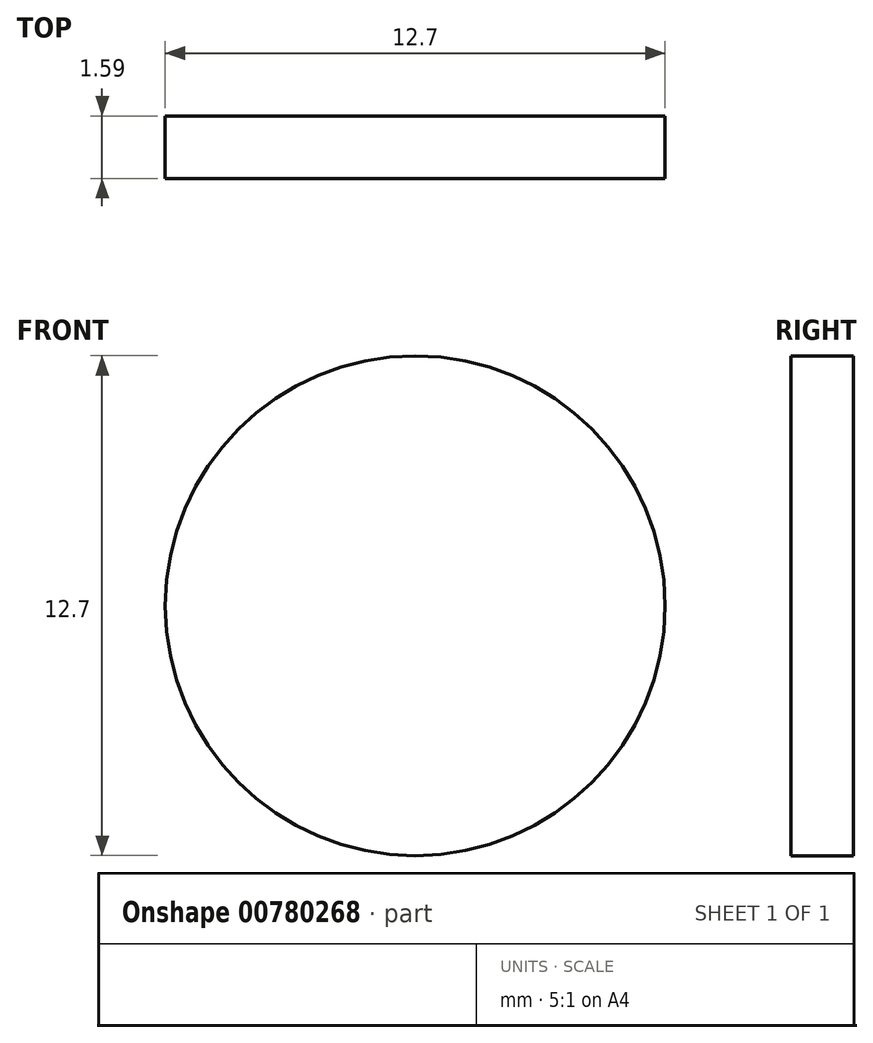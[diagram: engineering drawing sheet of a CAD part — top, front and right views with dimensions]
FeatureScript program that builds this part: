
annotation { "Feature Type Name" : "Feature", "Feature Type Description" : "" }
export const myFeature = defineFeature(function(context is Context, id is Id, definition is map)
    precondition{}
    {
        {
            var Q0;
            Q0=qCreatedBy(makeId("Front.planeOp"),FACE);
            var sketch = newSketch(context, id + "F0", { "sketchPlane" : qUnion([Q0])});
            skCircle(sketch, "E0", {"center": v(-222.34, -43.36) * mm, "radius": 6.35 * mm});
            skSolve(sketch);
        }
        {
            var Q0;
            Q0=makeQuery(id+"F0.imprint","IMPRINT",FACE,{"disambiguationData":[TD([[makeQuery(id+"F0.imprint","IMPRINT",EDGE,{"derivedFrom":sQuery(id+"F0.wireOp",EDGE,"E0")}),1.0]])]});
            extrude(context, id + "F1", {"entities" : qUnion([Q0]), "oppositeDirection" : true, "depth" : 1.59 * mm, "offsetDistance" : 25 * mm});
        }
    });
